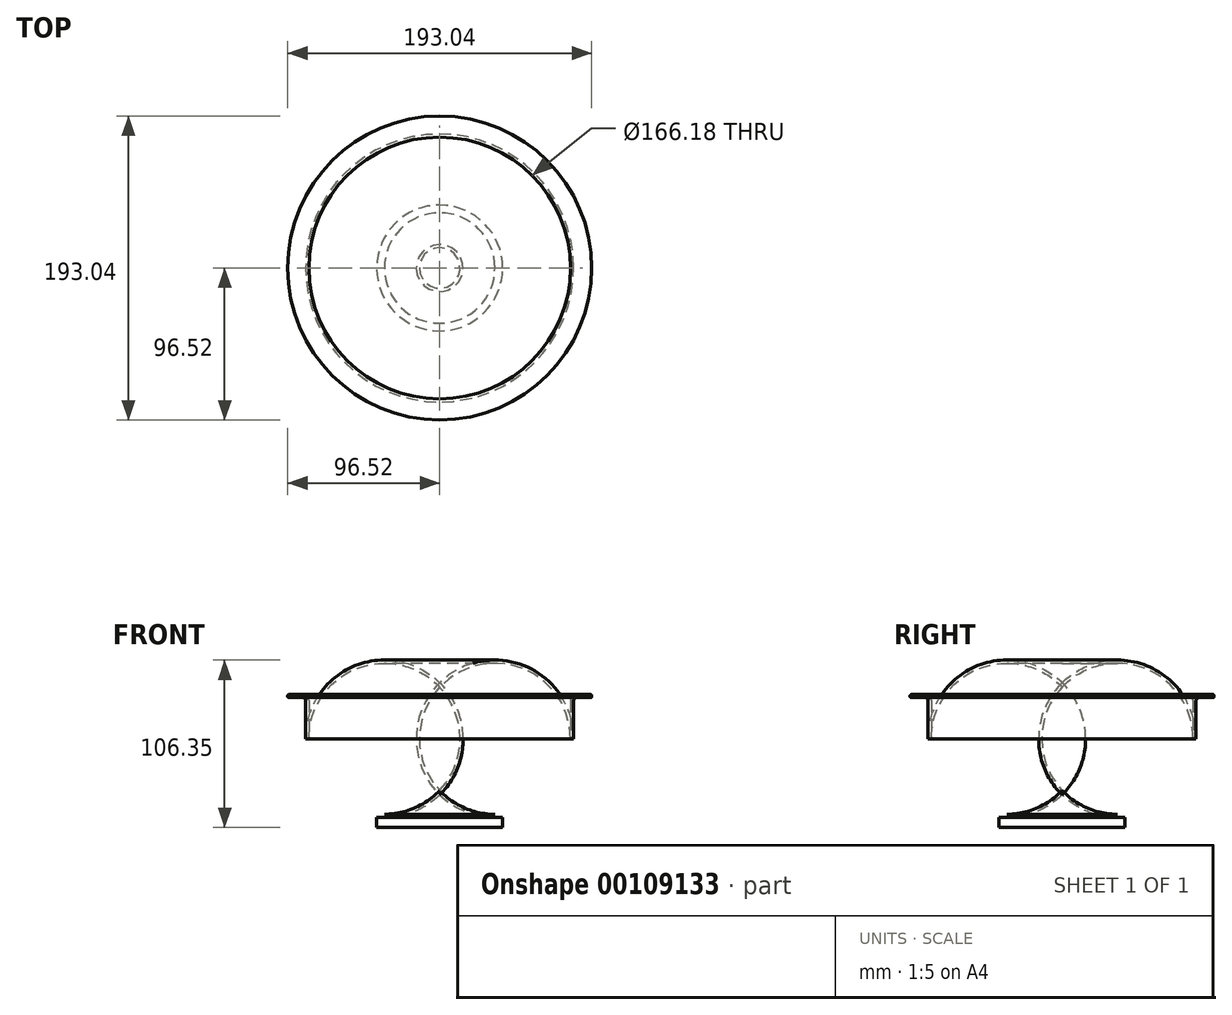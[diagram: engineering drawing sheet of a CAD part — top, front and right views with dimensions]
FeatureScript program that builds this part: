
annotation { "Feature Type Name" : "Feature", "Feature Type Description" : "" }
export const myFeature = defineFeature(function(context is Context, id is Id, definition is map)
    precondition{}
    {
        {
            var Q0;
            Q0=qCreatedBy(makeId("Top.planeOp"),FACE);
            var sketch = newSketch(context, id + "F0", { "sketchPlane" : qUnion([Q0])});
            skCircle(sketch, "E0", {"center": v(0, 0) * mm, "radius": 85.1 * mm});
            skSolve(sketch);
        }
        {
            var Q0;
            Q0=makeQuery(id+"F0.imprint","IMPRINT",FACE,{"disambiguationData":[TD([[makeQuery(id+"F0.imprint","IMPRINT",EDGE,{"derivedFrom":sQuery(id+"F0.wireOp",EDGE,"E0")}),1.0]])]});
            extrude(context, id + "F1", {"entities" : qUnion([Q0]), "depth" : 76.2 * mm});
        }
        {
            var Q0;
            Q0=makeQuery(id+"F1.opExtrude","CAP_FACE",FACE,{"disambiguationData":[OSD([sQuery(id+"F0.wireOp",EDGE,"E0")])],"isStart":false});
            var sketch = newSketch(context, id + "F2", { "sketchPlane" : qUnion([Q0])});
            skCircle(sketch, "E1", {"center": v(0, 0) * mm, "radius": 96.52 * mm});
            skSolve(sketch);
        }
        {
            var Q0;
            Q0=makeQuery(id+"F2.imprint","IMPRINT",FACE,{"disambiguationData":[TD([[makeQuery(id+"F2.imprint","IMPRINT",EDGE,{"derivedFrom":makeQuery(id+"F1.opExtrude","CAP_EDGE",EDGE,{"disambiguationData":[OSD([sQuery(id+"F0.wireOp",EDGE,"E0")])],"isStart":false})}),1.0]])]});
            var Q1;
            {var subQ0=sQuery(id+"F2.wireOp",EDGE,"G6rd5Lln-i4be-b8DC-3Qsr-jkEgab1qWMzD");Q1=makeQuery(id+"F2.imprint","IMPRINT",FACE,{"disambiguationData":[TD([[makeQuery(id+"F2.imprint","IMPRINT",EDGE,{"derivedFrom":subQ0}),1.0]])]});}
            var Q2;
            Q2=makeQuery(id+"F2.imprint","IMPRINT",FACE,{"disambiguationData":[TD([[makeQuery(id+"F2.imprint","IMPRINT",EDGE,{"derivedFrom":makeQuery(id+"F1.opExtrude","CAP_EDGE",EDGE,{"disambiguationData":[OSD([sQuery(id+"F0.wireOp",EDGE,"E0")])],"isStart":false})}),-1.0]])]});
            var Q3;
            {var subQ0=sQuery(id+"F2.wireOp",EDGE,"db650dfb-11c4-4845-aa70-980e46ba3c470.MirrorCS");Q3=makeQuery(id+"F2.imprint","IMPRINT",FACE,{"disambiguationData":[TD([[makeQuery(id+"F2.imprint","IMPRINT",EDGE,{"derivedFrom":subQ0}),-1.0]])]});}
            extrude(context, id + "F3", {"entities" : qUnion([Q0, Q1, Q2, Q3]), "operationType" : NewBodyOperationType.ADD, "depth" : 2 * mm});
        }
        {
            var Q0;
            Q0=makeQuery(id+"F1.opExtrude","CAP_FACE",FACE,{"disambiguationData":[OSD([sQuery(id+"F0.wireOp",EDGE,"E0")])],"isStart":true});
            fillet(context, id + "F4", {"entities" : qUnion([Q0]), "radius" : 50 * mm, "tangentPropagation" : true, "allowEdgeOverflow" : false});
        }
        {
            var Q0;
            Q0=makeQuery(id+"F1.opExtrude","SWEPT_FACE",FACE,{"disambiguationData":[OSD([sQuery(id+"F0.wireOp",EDGE,"E0")])]});
            fillet(context, id + "F5", {"entities" : qUnion([Q0]), "radius" : 2 * mm, "tangentPropagation" : true, "allowEdgeOverflow" : false});
        }
        {
            var Q0;
            Q0=makeQuery(id+"F3.opExtrude","CAP_FACE",FACE,{"disambiguationData":[OSD([sQuery(id+"F2.wireOp",EDGE,"E1"),sQuery(id+"F2.wireOp",EDGE,"G6rd5Lln-i4be-b8DC-3Qsr-jkEgab1qWMzD"),sQuery(id+"F2.wireOp",EDGE,"db650dfb-11c4-4845-aa70-980e46ba3c470.MirrorCS")])],"isStart":true});
            fillet(context, id + "F6", {"entities" : qUnion([Q0]), "radius" : 0.5 * mm, "tangentPropagation" : true, "allowEdgeOverflow" : false});
        }
        {
            var Q0;
            Q0=makeQuery(id+"F3.opExtrude","CAP_FACE",FACE,{"disambiguationData":[OSD([sQuery(id+"F2.wireOp",EDGE,"E1"),sQuery(id+"F2.wireOp",EDGE,"G6rd5Lln-i4be-b8DC-3Qsr-jkEgab1qWMzD"),sQuery(id+"F2.wireOp",EDGE,"db650dfb-11c4-4845-aa70-980e46ba3c470.MirrorCS")])],"isStart":false});
            fillet(context, id + "F7", {"entities" : qUnion([Q0]), "radius" : 1 * mm, "tangentPropagation" : true, "allowEdgeOverflow" : false});
        }
        {
            var Q0;
            Q0=makeQuery(id+"F3.opExtrude","CAP_FACE",FACE,{"disambiguationData":[OSD([sQuery(id+"F2.wireOp",EDGE,"E1"),sQuery(id+"F2.wireOp",EDGE,"G6rd5Lln-i4be-b8DC-3Qsr-jkEgab1qWMzD"),sQuery(id+"F2.wireOp",EDGE,"db650dfb-11c4-4845-aa70-980e46ba3c470.MirrorCS")])],"isStart":false});
            shell(context, id + "F8", {"entities" : qUnion([Q0]), "thickness" : 2 * mm});
        }
        {
            var Q0;
            Q0=makeQuery(id+"F1.opExtrude","CAP_FACE",FACE,{"disambiguationData":[OSD([sQuery(id+"F0.wireOp",EDGE,"E0")])],"isStart":true});
            var sketch = newSketch(context, id + "F9", { "sketchPlane" : qUnion([Q0])});
            skCircle(sketch, "E2", {"center": v(0, 0) * mm, "radius": 40 * mm});
            skSolve(sketch);
        }
        {
            var Q0;
            Q0=makeQuery(id+"F9.imprint","IMPRINT",FACE,{"disambiguationData":[TD([[makeQuery(id+"F9.imprint","IMPRINT",EDGE,{"derivedFrom":sQuery(id+"F9.wireOp",EDGE,"E2")}),1.0]])]});
            var Q1;
            {var subQ0=sQuery(id+"F0.wireOp",EDGE,"E0");Q1=makeQuery(id+"F9.imprint","IMPRINT",FACE,{"disambiguationData":[TD([[makeQuery(id+"F9.imprint","IMPRINT",EDGE,{"derivedFrom":makeQuery(id+"F4.opFillet","BLEND_EDGE",EDGE,{"blendedFrom":[makeQuery(id+"F1.opExtrude","CAP_EDGE",EDGE,{"disambiguationData":[OSD([subQ0])],"isStart":true}),makeQuery(id+"F1.opExtrude","CAP_FACE",FACE,{"disambiguationData":[OSD([subQ0])],"isStart":true})],"blendedInto":[makeQuery(id+"F1.opExtrude","CAP_FACE",FACE,{"disambiguationData":[OSD([subQ0])],"isStart":true})]})}),1.0]])]});}
            extrude(context, id + "F10", {"entities" : qUnion([Q0, Q1]), "operationType" : NewBodyOperationType.ADD, "depth" : 6.35 * mm});
        }
    });
